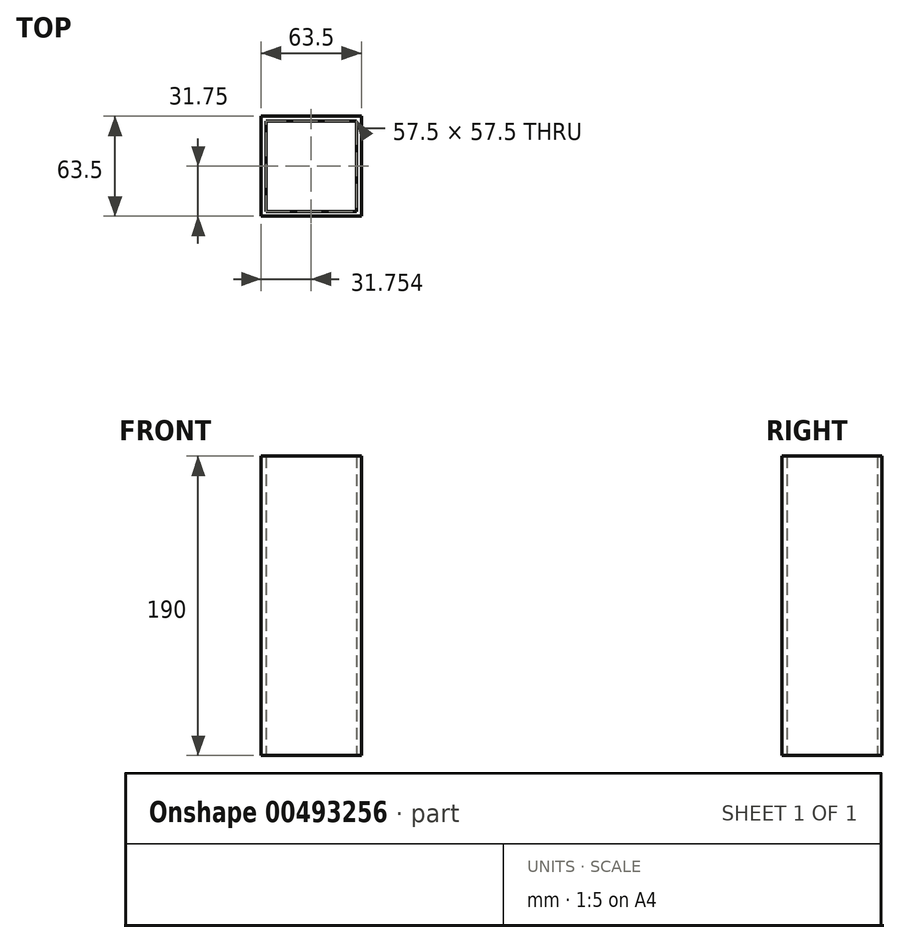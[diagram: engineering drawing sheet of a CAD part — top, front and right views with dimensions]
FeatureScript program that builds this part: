
annotation { "Feature Type Name" : "Feature", "Feature Type Description" : "" }
export const myFeature = defineFeature(function(context is Context, id is Id, definition is map)
    precondition{}
    {
        {
            var Q0;
            Q0=qCreatedBy(makeId("Top.planeOp"),FACE);
            var sketch = newSketch(context, id + "F0", { "sketchPlane" : qUnion([Q0])});
            skLineSegment(sketch, "E0.bottom", {"start": v(-85.74, 19.43) * mm, "end": v(-28.24, 19.43) * mm});
            skLineSegment(sketch, "E0.top", {"start": v(-85.74, -38.07) * mm, "end": v(-28.24, -38.07) * mm});
            skLineSegment(sketch, "E0.left", {"start": v(-85.74, 19.43) * mm, "end": v(-85.74, -38.07) * mm});
            skLineSegment(sketch, "E0.right", {"start": v(-28.24, 19.43) * mm, "end": v(-28.24, -38.07) * mm});
            skLineSegment(sketch, "E1.bottom", {"start": v(-88.74, 22.43) * mm, "end": v(-25.24, 22.43) * mm});
            skLineSegment(sketch, "E1.top", {"start": v(-88.74, -41.07) * mm, "end": v(-25.24, -41.07) * mm});
            skLineSegment(sketch, "E1.left", {"start": v(-88.74, 22.43) * mm, "end": v(-88.74, -41.07) * mm});
            skLineSegment(sketch, "E1.right", {"start": v(-25.24, 22.43) * mm, "end": v(-25.24, -41.07) * mm});
            skSolve(sketch);
        }
        {
            var Q0;
            Q0=qSketchRegion(id+"F0",true);
            extrude(context, id + "F1", {"entities" : qUnion([Q0]), "depth" : 190 * mm});
        }
    });
